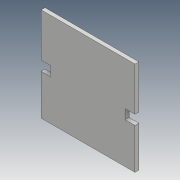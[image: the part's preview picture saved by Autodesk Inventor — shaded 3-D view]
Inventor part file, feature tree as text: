
AUTODESK INVENTOR PART (.ipt)
format: ipt  version: 2017 (Build 210142000, 142)  size: 95,744 bytes
history: native  units: mm
features: extrude x2, sketch x2
ambient origin geometry x8: Origin, YZ Plane, XZ Plane, XY Plane, X Axis, Y Axis, Z Axis, Center Point
bodies: Solid1 (feature_tree)
feature tree (4):
  extrude  "Extrusion1"  Depth=49.0mm
  extrude  "Extrusion4"  Depth=5.0mm
  sketch  "Sketch1"  dims[d0=49.0mm d1=49.0mm]
  sketch  "Sketch5"  dims[d2=2.0mm d3=0.0mm d39=5.0mm d40=39.0mm d41=5.0mm d42=10.0mm d43=0.0mm]
